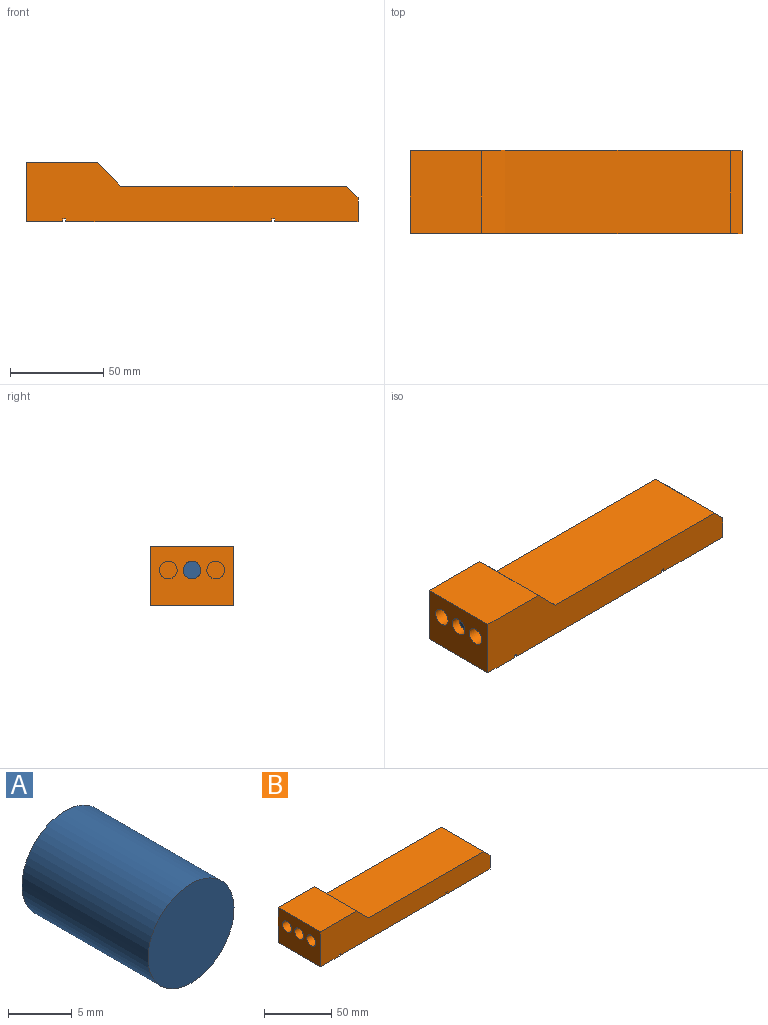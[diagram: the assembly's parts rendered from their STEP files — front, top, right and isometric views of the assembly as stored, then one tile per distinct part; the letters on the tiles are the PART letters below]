
ASSEMBLY  parts=2 mates=1
PART A: 3 faces, bbox 9.5x14x9.5 mm
  f0: cylinder r=4.76mm len=13.97mm, axis (0,1,0), area 418mm2, adj f1,f2
  f1: plane 9.53x9.53mm, normal (0,-1,0), area 71.3mm2, adj f0
  f2: plane 9.53x9.53mm, normal (0,1,0), area 71.3mm2, adj f0
PART B: 23 faces, bbox 177.8x44.5x31.8 mm
  f0: plane 44.45x12.7mm, normal (1,0,0), area 564.5mm2, adj f1,f2,f13,f16
  f1: plane 177.8x31.75mm, normal (0,-1,0), area 3926.4mm2, adj f0,f3,f4,f5,f6,f7,f8,f9
  f2: plane 177.8x31.75mm, normal (0,1,0), area 3926.4mm2, adj f0,f3,f4,f5,f6,f7,f8,f9
  f3: plane 44.45x38.1mm, normal (0,0,1), area 1693.5mm2, adj f1,f2,f4,f15
  f4: plane 44.45x31.75mm, normal (-1,0,0), area 1197.5mm2, adj f1,f2,f3,f5,f17,f19,f21
  f5: plane 44.45x19.78mm, normal (0,0,-1), area 879.2mm2, adj f1,f2,f4,f6
  f6: plane 44.45x1.59mm, normal (1,0,0), area 70.6mm2, adj f1,f2,f5,f7
  f7: plane 44.45x1.59mm, normal (0,0,-1), area 70.6mm2, adj f1,f2,f6,f8
  f8: plane 44.45x1.59mm, normal (-1,0,0), area 70.6mm2, adj f1,f2,f7,f9
  f9: plane 110.17x44.45mm, normal (0,0,-1), area 4897.2mm2, adj f1,f2,f8,f10
  f10: plane 44.45x1.59mm, normal (1,0,0), area 70.6mm2, adj f1,f2,f9,f11
  f11: plane 44.45x1.59mm, normal (0,0,-1), area 70.6mm2, adj f1,f2,f10,f12
  f12: plane 44.45x1.59mm, normal (-1,0,0), area 70.6mm2, adj f1,f2,f11,f13
  f13: plane 44.67x44.45mm, normal (0,0,-1), area 1985.7mm2, adj f0,f1,f2,f12
  f14: plane 120.65x44.45mm, normal (0,0,1), area 5362.9mm2, adj f1,f2,f15,f16
  f15: plane 44.45x12.7mm, normal (0.71,0,0.71), area 798.3mm2, adj f1,f2,f3,f14
  f16: plane 44.45x6.35mm, normal (0.71,0,0.71), area 399.2mm2, adj f0,f1,f2,f14
  f17: cylinder r=4.76mm len=19.05mm, axis (-1,0,0), area 570mm2, adj f4,f18
  f18: plane 9.53x9.53mm, normal (-1,0,0), area 71.3mm2, adj f17
  f19: cylinder r=4.76mm len=19.05mm, axis (-1,0,0), area 570mm2, adj f4,f20
  f20: plane 9.53x9.53mm, normal (-1,0,0), area 71.3mm2, adj f19
  f21: cylinder r=4.76mm len=19.05mm, axis (-1,0,0), area 570mm2, adj f4,f22
  f22: plane 9.53x9.53mm, normal (-1,0,0), area 71.3mm2, adj f21
PLACE A rot(axis=(0.58,-0.58,0.58),120deg) t=(-49.22,37.9,30.06)mm
PLACE B t=(-33.73,37.9,11.01)mm
MATE cylindrical A.f0 <-> B.f17  axis (1,0,0) through (-35.25,37.9,30.06)mm
